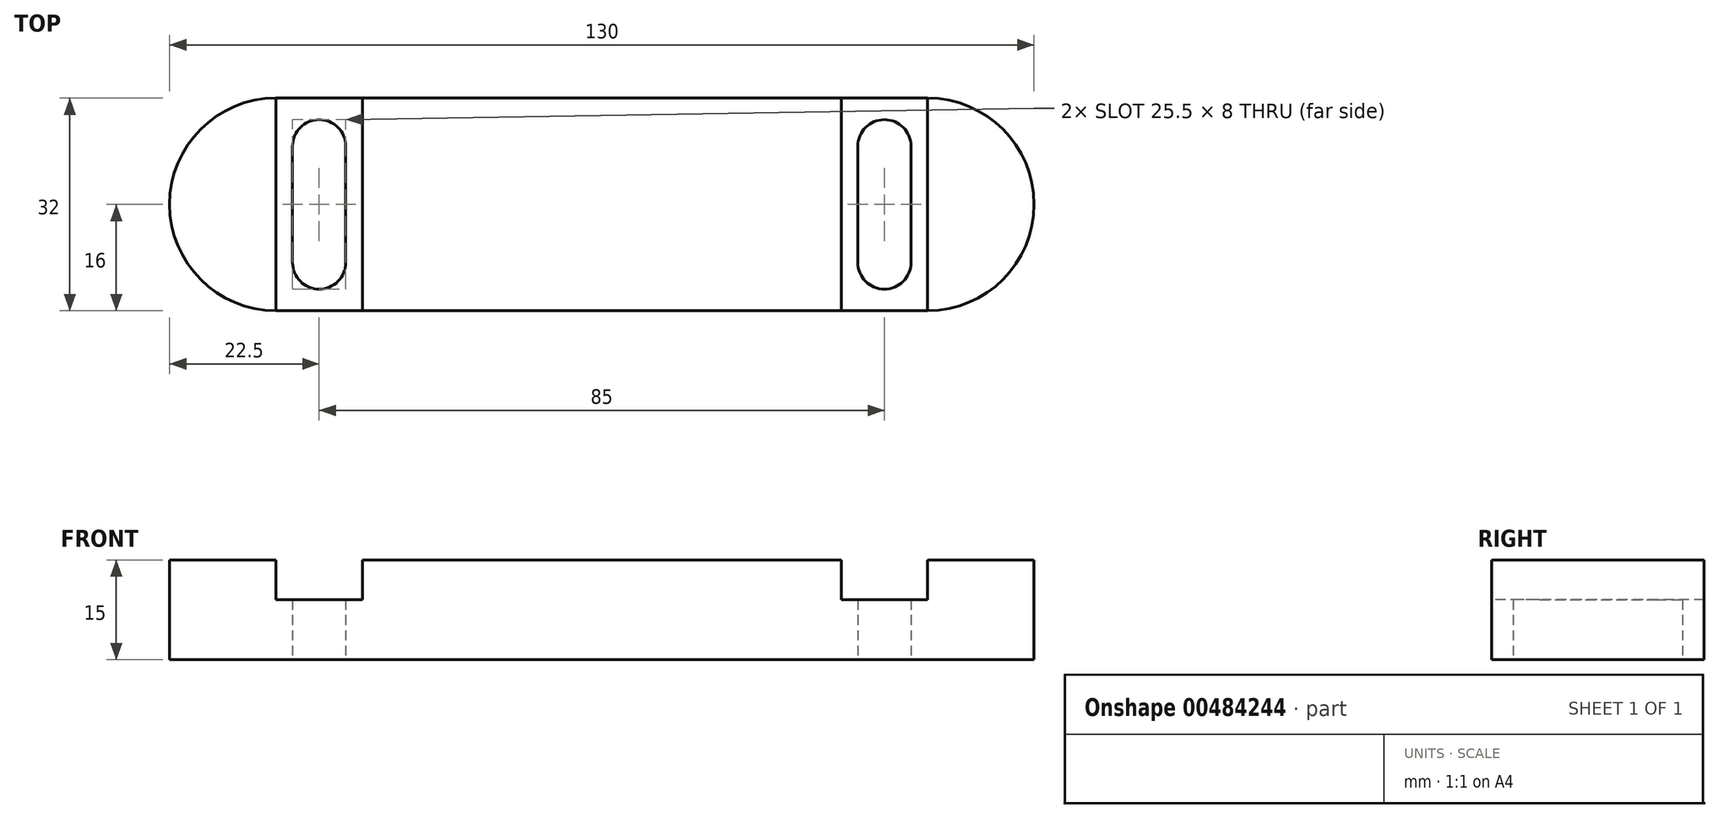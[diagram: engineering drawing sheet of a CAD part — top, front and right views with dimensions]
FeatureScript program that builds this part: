
annotation { "Feature Type Name" : "Feature", "Feature Type Description" : "" }
export const myFeature = defineFeature(function(context is Context, id is Id, definition is map)
    precondition{}
    {
        {
            var Q0;
            Q0=qCreatedBy(makeId("Top.planeOp"),FACE);
            var sketch = newSketch(context, id + "F0", { "sketchPlane" : qUnion([Q0])});
            skLineSegment(sketch, "E0", {"start": v(0, 16) * mm, "end": v(0, -16) * mm, "construction": true});
            skLineSegment(sketch, "E1", {"start": v(0, 16) * mm, "end": v(-49, 16) * mm});
            skLineSegment(sketch, "E2", {"start": v(0, -16) * mm, "end": v(-49, -16) * mm});
            skArc(sketch, "E3", {"start": v(-49, 16) * mm, "mid": v(-65, 0) * mm, "end": v(-49, -16) * mm});
            skLineSegment(sketch, "E4", {"start": v(-46.5, 8.75) * mm, "end": v(-46.5, -8.75) * mm});
            skLineSegment(sketch, "E5", {"start": v(-38.5, -8.75) * mm, "end": v(-38.5, 8.75) * mm});
            skArc(sketch, "E6", {"start": v(-46.5, -8.75) * mm, "mid": v(-42.5, -12.75) * mm, "end": v(-38.5, -8.75) * mm});
            skArc(sketch, "E7", {"start": v(-38.5, 8.75) * mm, "mid": v(-42.5, 12.75) * mm, "end": v(-46.5, 8.75) * mm});
            skLineSegment(sketch, "E8", {"start": v(-49, 16) * mm, "end": v(-49, -16) * mm, "construction": true});
            skLineSegment(sketch, "E9", {"start": v(-36, 16) * mm, "end": v(-36, -16) * mm, "construction": true});
            skLineSegment(sketch, "E10", {"start": v(-38.5, 0) * mm, "end": v(-46.5, 0) * mm, "construction": true});
            skPoint(sketch, "E11", {"position": v(-42.5, 0) * mm});
            skPoint(sketch, "E12", {"position": v(-42.5, 16) * mm});
            skLineSegment(sketch, "E13.MirrorCS", {"start": v(0, -16) * mm, "end": v(49, -16) * mm});
            skLineSegment(sketch, "E14.MirrorCS", {"start": v(38.5, -8.75) * mm, "end": v(38.5, 8.75) * mm});
            skArc(sketch, "E15.MirrorCS", {"start": v(46.5, -8.75) * mm, "mid": v(42.5, -12.75) * mm, "end": v(38.5, -8.75) * mm});
            skLineSegment(sketch, "E16.MirrorCS", {"start": v(38.5, 0) * mm, "end": v(46.5, 0) * mm, "construction": true});
            skPoint(sketch, "E17.MirrorP", {"position": v(42.5, 16) * mm});
            skPoint(sketch, "E18.MirrorP", {"position": v(42.5, 0) * mm});
            skLineSegment(sketch, "E19.MirrorCS", {"start": v(0, 16) * mm, "end": v(49, 16) * mm});
            skLineSegment(sketch, "E20.MirrorCS", {"start": v(46.5, 8.75) * mm, "end": v(46.5, -8.75) * mm});
            skArc(sketch, "E21.MirrorCS", {"start": v(49, 16) * mm, "mid": v(65, 0) * mm, "end": v(49, -16) * mm});
            skLineSegment(sketch, "E22.MirrorCS", {"start": v(49, 16) * mm, "end": v(49, -16) * mm, "construction": true});
            skArc(sketch, "E23.MirrorCS", {"start": v(38.5, 8.75) * mm, "mid": v(42.5, 12.75) * mm, "end": v(46.5, 8.75) * mm});
            skLineSegment(sketch, "E24.MirrorCS", {"start": v(36, 16) * mm, "end": v(36, -16) * mm, "construction": true});
            skSolve(sketch);
        }
        {
            var Q0;
            Q0 = qSketchRegion(id + "F0", true);
            extrude(context, id + "F1", {"entities" : qUnion([Q0]), "depth" : 15 * mm});
        }
        {
            var Q0;
            Q0=makeQuery(id+"F1.opExtrude","CAP_FACE",FACE,{"disambiguationData":[OSD([sQuery(id+"F0.wireOp",EDGE,"E1"),sQuery(id+"F0.wireOp",EDGE,"E2"),sQuery(id+"F0.wireOp",EDGE,"E3"),sQuery(id+"F0.wireOp",EDGE,"E4"),sQuery(id+"F0.wireOp",EDGE,"E5"),sQuery(id+"F0.wireOp",EDGE,"E6"),sQuery(id+"F0.wireOp",EDGE,"E7"),sQuery(id+"F0.wireOp",EDGE,"E13.MirrorCS"),sQuery(id+"F0.wireOp",EDGE,"E14.MirrorCS"),sQuery(id+"F0.wireOp",EDGE,"E15.MirrorCS"),sQuery(id+"F0.wireOp",EDGE,"E19.MirrorCS"),sQuery(id+"F0.wireOp",EDGE,"E20.MirrorCS"),sQuery(id+"F0.wireOp",EDGE,"E21.MirrorCS"),sQuery(id+"F0.wireOp",EDGE,"E23.MirrorCS")])],"isStart":false});
            var sketch = newSketch(context, id + "F2", { "sketchPlane" : qUnion([Q0])});
            skLineSegment(sketch, "E25", {"start": v(-49, 16) * mm, "end": v(-49, -16) * mm});
            skLineSegment(sketch, "E26", {"start": v(-36, 16) * mm, "end": v(-36, -16) * mm});
            skLineSegment(sketch, "E27.MirrorCS", {"start": v(49, 16) * mm, "end": v(49, -16) * mm});
            skLineSegment(sketch, "E28.MirrorCS", {"start": v(36, 16) * mm, "end": v(36, -16) * mm});
            skSolve(sketch);
        }
        {
            var Q0;
            {var subQ0=sQuery(id+"F2.wireOp",EDGE,"E25");Q0=makeQuery(id+"F2.imprint","IMPRINT",FACE,{"disambiguationData":[TD([[makeQuery(id+"F2.imprint","IMPRINT",EDGE,{"derivedFrom":subQ0}),1.0]])]});}
            var Q1;
            {var subQ1=sQuery(id+"F2.wireOp",EDGE,"E27.MirrorCS");Q1=makeQuery(id+"F2.imprint","IMPRINT",FACE,{"disambiguationData":[TD([[makeQuery(id+"F2.imprint","IMPRINT",EDGE,{"derivedFrom":subQ1}),-1.0]])]});}
            extrude(context, id + "F3", {"entities" : qUnion([Q0, Q1]), "operationType" : NewBodyOperationType.REMOVE, "oppositeDirection" : true, "depth" : 6 * mm});
        }
    });
